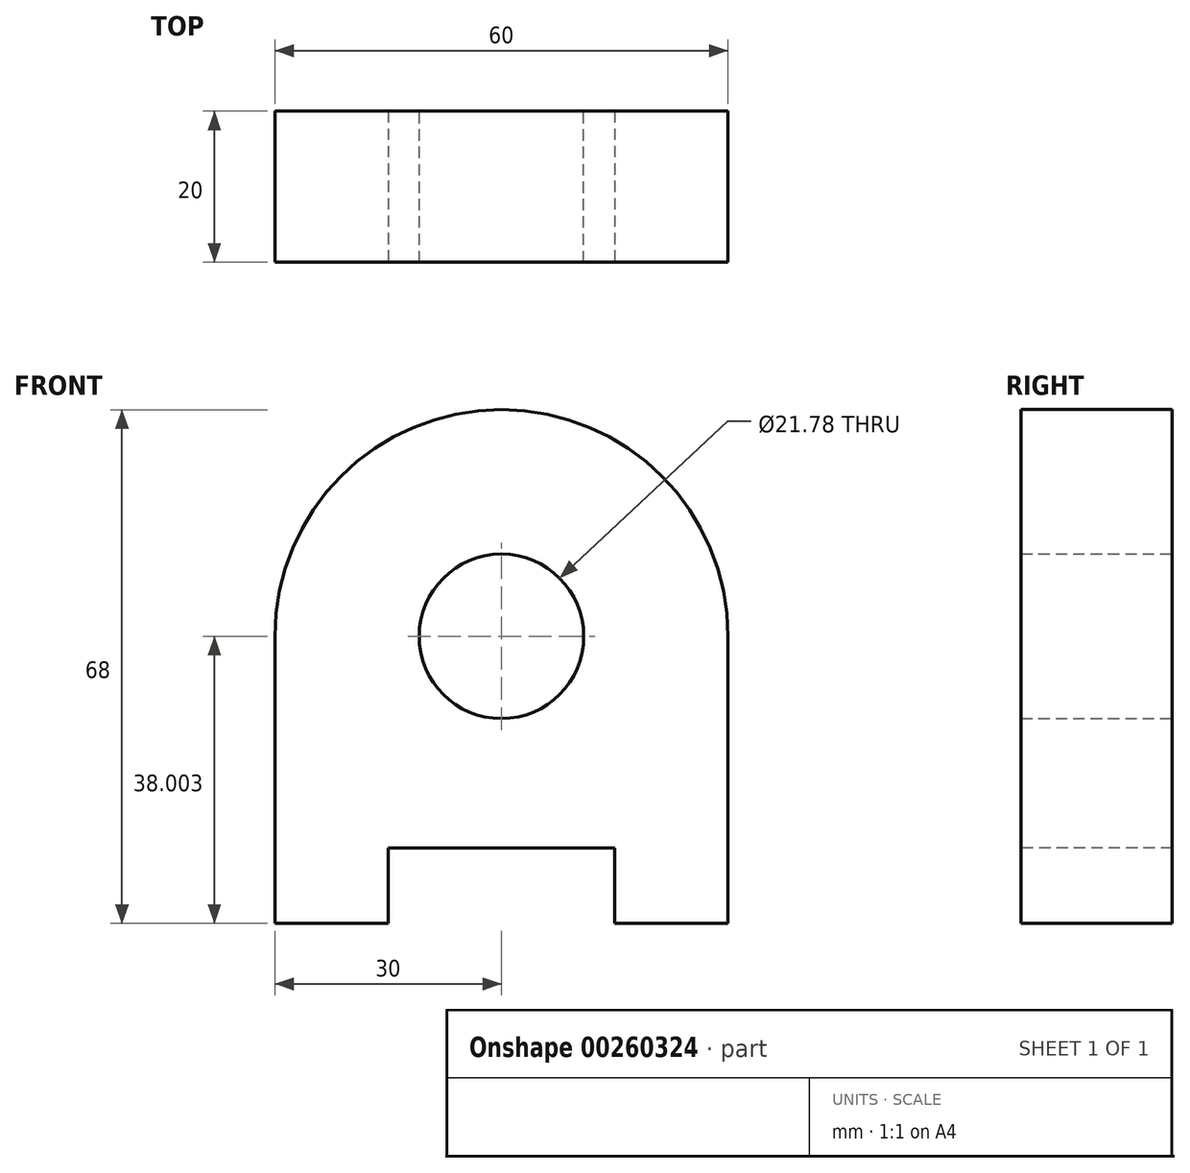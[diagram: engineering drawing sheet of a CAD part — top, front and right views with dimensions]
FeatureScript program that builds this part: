
annotation { "Feature Type Name" : "Feature", "Feature Type Description" : "" }
export const myFeature = defineFeature(function(context is Context, id is Id, definition is map)
    precondition{}
    {
        {
            var Q0;
            Q0=qCreatedBy(makeId("Front.planeOp"),FACE);
            var sketch = newSketch(context, id + "F0", { "sketchPlane" : qUnion([Q0])});
            skLineSegment(sketch, "E0", {"start": v(-60, 22.05) * mm, "end": v(-60, -15.95) * mm});
            skLineSegment(sketch, "E1", {"start": v(-60, -15.95) * mm, "end": v(0, -15.95) * mm});
            skLineSegment(sketch, "E2", {"start": v(0, -15.95) * mm, "end": v(0, 22.05) * mm});
            skArc(sketch, "E3", {"start": v(0, 22.05) * mm, "mid": v(-30, 52.05) * mm, "end": v(-60, 22.05) * mm});
            skCircle(sketch, "E4", {"center": v(-30, 22.05) * mm, "radius": 10.89 * mm});
            skSolve(sketch);
        }
        {
            var Q0;
            Q0=makeQuery(id+"F0.imprint","IMPRINT",FACE,{"disambiguationData":[TD([[makeQuery(id+"F0.imprint","IMPRINT",EDGE,{"derivedFrom":sQuery(id+"F0.wireOp",EDGE,"E0")}),1.0]])]});
            extrude(context, id + "F1", {"entities" : qUnion([Q0]), "depth" : 20 * mm});
        }
        {
            var Q0;
            Q0=makeQuery(id+"F1.opExtrude","CAP_FACE",FACE,{"disambiguationData":[OSD([sQuery(id+"F0.wireOp",EDGE,"E0"),sQuery(id+"F0.wireOp",EDGE,"E1"),sQuery(id+"F0.wireOp",EDGE,"E2"),sQuery(id+"F0.wireOp",EDGE,"E3"),sQuery(id+"F0.wireOp",EDGE,"E4")])],"isStart":false});
            var sketch = newSketch(context, id + "F2", { "sketchPlane" : qUnion([Q0])});
            skLineSegment(sketch, "E5", {"start": v(0, -15.95) * mm, "end": v(-15, -15.95) * mm});
            skLineSegment(sketch, "E6", {"start": v(-60, -15.95) * mm, "end": v(-45, -15.95) * mm});
            skLineSegment(sketch, "E7", {"start": v(-45, -15.95) * mm, "end": v(-45, -5.95) * mm});
            skLineSegment(sketch, "E8", {"start": v(-45, -5.95) * mm, "end": v(-15, -5.95) * mm});
            skLineSegment(sketch, "E9", {"start": v(-15, -5.95) * mm, "end": v(-15, -15.95) * mm});
            skSolve(sketch);
        }
        {
            var Q0;
            Q0 = qSketchRegion(id + "F2", true);
            var Q1;
            {var subQ0=sQuery(id+"F2.wireOp",EDGE,"E7");Q1=makeQuery(id+"F2.imprint","IMPRINT",FACE,{"disambiguationData":[TD([[makeQuery(id+"F2.imprint","IMPRINT",EDGE,{"derivedFrom":subQ0}),-1.0]])]});}
            extrude(context, id + "F3", {"entities" : qUnion([Q0, Q1]), "operationType" : NewBodyOperationType.REMOVE, "endBound" : BoundingType.THROUGH_ALL, "oppositeDirection" : true, "depth" : 25 * mm});
        }
    });
